# Revit family: BE_50673.1_de_DE
name_source: partatom
category: Leuchten
units: mm (PartAtom-declared; Revit-internal decimal feet)

## family parameters
Basisbauteil = Fläche
Beim Laden mit Abzugskörper schneiden = Ja
Bemaßung runder Anschluss = Durchmesser verwenden
Gemeinsam genutzt = Nein
Lichtquelle = Nein
Raumberechnungspunkt = Ja
Teiletyp = Normal

## types (2) — shared parameters
AC/DC = AC/DC
Aktualisierung = 2023-04-19T04:00:03
Beschreibung = Großraum-Pendelleuchte
Beschreibung_Sonderanfertigung = Hier können Sie Informationen zur Sonderanfertigung eintragen.
CE_Konformität = ja
ENEC = ja
Energieeffizienzklasse = LED A++ - A
Farbwiedergabeindex = CRI > 90
Frequenz = 0/50-60 Hz
Gewicht = 12.0 kg
Hersteller = BEGA
Lampe = LED 121.2 W
Lastklassifizierung = Beleuchtung
Lebensdauerkriterien = L70B50 @ 25 °C = 120000 h
Logo = BEGA_Logo.png
Material_03 = BEGA_Oberfläche_Weiss_matt
Material_11 = BEGA_Glas_opal
Material_17 = BEGA_Reflektor
Material_22 = BEGA_Oberfläche_Aluminium_matt
Produktdatenblatt = https://cdn.bega.com
Scheinlast = 0 VA
Schutzart = IP 20
Schutzklasse = I
Sonderanfertigung = Nein
Spannung = 240 V
URL = https://www.bega.com
Umgebungstemperatur = 25 °C
zero-valued in all types: Vorgabe-Ansicht

## per-type parameters (varying)
| type | BEGA_IES1 | BEGA_IES2 | Bestellnummer | Farbtemperatur | LED_Modulbezeichnung | Lampenlichtstrom | Leuchtenlichtstrom | Modell |
| BEGA_50673.1_Weiß_K3 | Ja | Nein | 50673.1K3 | 3000 K | LED-0694/930 | 19060 lm | 14130 lm | 50673.1K3 |
| BEGA_50673.1_Weiß_K4 | Nein | Ja | 50673.1K4 | 4000 K | LED-0694/940 | 20060 lm | 14567 lm | 50673.1K4 |

## geometry (parser evidence)
native form markers: Blend x16, Sweep x6
no freeform markers — native parametric forms only
